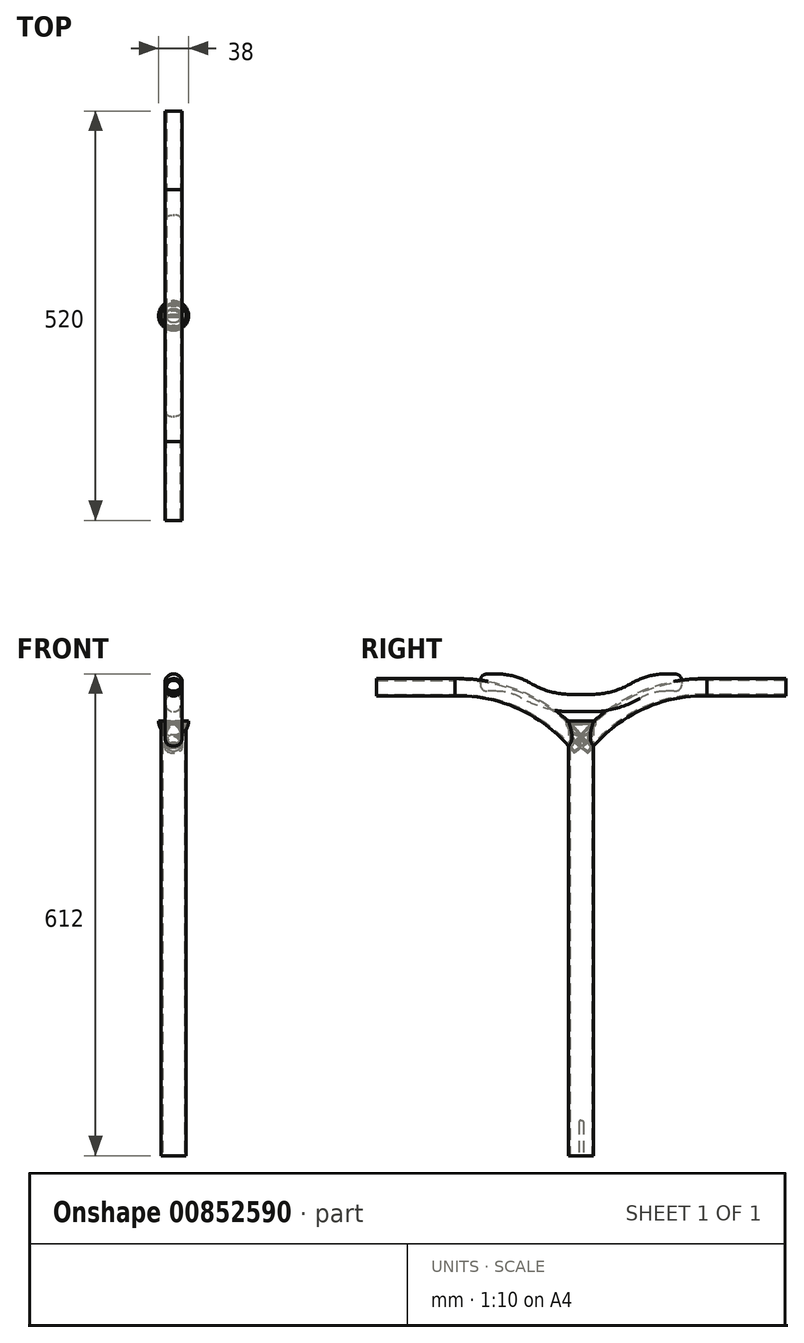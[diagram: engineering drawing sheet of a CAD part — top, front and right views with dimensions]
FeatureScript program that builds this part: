
annotation { "Feature Type Name" : "Feature", "Feature Type Description" : "" }
export const myFeature = defineFeature(function(context is Context, id is Id, definition is map)
    precondition{}
    {
        {
            var Q0;
            Q0=qCreatedBy(makeId("Top.planeOp"),FACE);
            var sketch = newSketch(context, id + "F0", { "sketchPlane" : qUnion([Q0])});
            skCircle(sketch, "E0", {"center": v(0, 0) * mm, "radius": 16 * mm});
            skSolve(sketch);
        }
        {
            var Q0;
            Q0=makeQuery(id+"F0.imprint","IMPRINT",FACE,{"disambiguationData":[TD([[makeQuery(id+"F0.imprint","IMPRINT",EDGE,{"derivedFrom":sQuery(id+"F0.wireOp",EDGE,"E0")}),1.0]])]});
            extrude(context, id + "F1", {"entities" : qUnion([Q0]), "depth" : 550 * mm, "offsetDistance" : 25 * mm});
        }
        {
            var Q0;
            Q0=makeQuery(id+"F1.opExtrude","CAP_FACE",FACE,{"disambiguationData":[OSD([sQuery(id+"F0.wireOp",EDGE,"E0")])],"isStart":true});
            shell(context, id + "F2", {"entities" : qUnion([Q0]), "thickness" : 2 * mm});
        }
        {
            var Q0;
            Q0=qCreatedBy(makeId("Right.planeOp"),FACE);
            var sketch = newSketch(context, id + "F3", { "sketchPlane" : qUnion([Q0])});
            skLineSegment(sketch, "E1.bottom", {"start": v(-2.92, 0) * mm, "end": v(3.08, 0) * mm});
            skLineSegment(sketch, "E1.top", {"start": v(0.08, 45) * mm, "end": v(0.08, 45) * mm});
            skLineSegment(sketch, "E1.left", {"start": v(-2.92, 0) * mm, "end": v(-2.92, 42) * mm});
            skLineSegment(sketch, "E1.right", {"start": v(3.08, 0) * mm, "end": v(3.08, 42) * mm});
            skPoint(sketch, "E2.visualSharp", {"position": v(-2.92, 45) * mm});
            skArc(sketch, "E2.filletArc", {"start": v(0.08, 45) * mm, "mid": v(-2.05, 44.12) * mm, "end": v(-2.92, 42) * mm});
            skPoint(sketch, "E3.visualSharp", {"position": v(3.08, 45) * mm});
            skArc(sketch, "E3.filletArc", {"start": v(3.08, 42) * mm, "mid": v(2.2, 44.12) * mm, "end": v(0.08, 45) * mm});
            skSolve(sketch);
        }
        {
            var Q0;
            Q0 = qSketchRegion(id + "F3", true);
            extrude(context, id + "F4", {"entities" : qUnion([Q0]), "operationType" : NewBodyOperationType.REMOVE, "endBound" : BoundingType.THROUGH_ALL, "oppositeDirection" : true, "depth" : 25 * mm, "offsetDistance" : 25 * mm});
        }
        {
            var Q0;
            Q0=qCreatedBy(makeId("Right.planeOp"),FACE);
            var sketch = newSketch(context, id + "F5", { "sketchPlane" : qUnion([Q0])});
            skArc(sketch, "E4", {"start": v(160, 594.94) * mm, "mid": v(70.74, 575.74) * mm, "end": v(0, 518) * mm});
            skLineSegment(sketch, "E5", {"start": v(160, 594.94) * mm, "end": v(260, 594.94) * mm});
            skSolve(sketch);
        }
        {
            var Q0;
            Q0=qCreatedBy(makeId("Front.planeOp"),FACE);
            var Q1;
            Q1=sQuery(id+"F5.wireOp",VERTEX,"E5.end");
            cPlane(context, id + "F6", {"entities" : qUnion([Q0, Q1]), "cplaneType" : CPlaneType.PLANE_POINT, "offset" : 25 * mm, "width" : 150 * mm, "height" : 150 * mm});
        }
        {
            var Q0;
            Q0=qCreatedBy(id+"F6.planeOp",FACE);
            var sketch = newSketch(context, id + "F7", { "sketchPlane" : qUnion([Q0])});
            skCircle(sketch, "E6", {"center": v(0, 594.94) * mm, "radius": 11 * mm});
            skSolve(sketch);
        }
        {
            var Q0;
            Q0=makeQuery(id+"F7.imprint","IMPRINT",FACE,{"disambiguationData":[TD([[makeQuery(id+"F7.imprint","IMPRINT",EDGE,{"derivedFrom":sQuery(id+"F7.wireOp",EDGE,"E6")}),1.0]])]});
            var Q1;
            Q1=sQuery(id+"F7.wireOp",EDGE,"E6");
            var Q2;
            Q2=sQuery(id+"F5.wireOp",EDGE,"E5");
            var Q3;
            Q3=sQuery(id+"F5.wireOp",EDGE,"E4");
            sweep(context, id + "F8", {"operationType" : NewBodyOperationType.ADD, "profiles" : qUnion([Q0]), "surfaceProfiles" : qUnion([Q1]), "path" : qUnion([Q2, Q3])});
        }
        {
            var Q0;
            Q0=makeQuery(id+"F8.opSweep","CAP_FACE",FACE,{"disambiguationData":[OSD([sQuery(id+"F5.wireOp",VERTEX,"E5.end"),sQuery(id+"F7.wireOp",EDGE,"E6")])],"isStart":true});
            shell(context, id + "F9", {"entities" : qUnion([Q0]), "thickness" : 2 * mm});
        }
        {
            var Q0;
            Q0=makeQuery(id+"F1.opExtrude","SWEPT_BODY",BODY,{"disambiguationData":[OSD([sQuery(id+"F0.wireOp",EDGE,"E0")])]});
            var Q1;
            Q1=qCreatedBy(makeId("Front.planeOp"),FACE);
            mirror(context, id + "F10", {"operationType" : NewBodyOperationType.ADD, "entities" : qUnion([Q0]), "mirrorPlane" : qUnion([Q1])});
        }
        {
            var Q0;
            Q0=qCreatedBy(makeId("Right.planeOp"),FACE);
            var sketch = newSketch(context, id + "F11", { "sketchPlane" : qUnion([Q0])});
            skArc(sketch, "E7", {"start": v(-69.28, 590.46) * mm, "mid": v(-41.92, 578.93) * mm, "end": v(-12.5, 575) * mm});
            skLineSegment(sketch, "E8", {"start": v(-12.5, 575) * mm, "end": v(0, 575) * mm});
            skArc(sketch, "E9", {"start": v(-69.28, 590.46) * mm, "mid": v(-87.93, 598.32) * mm, "end": v(-108, 601) * mm});
            skLineSegment(sketch, "E10", {"start": v(-108, 601) * mm, "end": v(-128, 601) * mm});
            skLineSegment(sketch, "E11.MirrorCS", {"start": v(12.5, 575) * mm, "end": v(0, 575) * mm});
            skArc(sketch, "E12.MirrorCS", {"start": v(69.28, 590.46) * mm, "mid": v(41.92, 578.93) * mm, "end": v(12.5, 575) * mm});
            skArc(sketch, "E13.MirrorCS", {"start": v(69.28, 590.46) * mm, "mid": v(87.93, 598.32) * mm, "end": v(108, 601) * mm});
            skLineSegment(sketch, "E14.MirrorCS", {"start": v(108, 601) * mm, "end": v(128, 601) * mm});
            skSolve(sketch);
        }
        {
            var Q0;
            Q0=sQuery(id+"F11.wireOp",VERTEX,"E14.MirrorCS.end");
            var Q1;
            Q1=qCreatedBy(id+"F6.planeOp",FACE);
            cPlane(context, id + "F12", {"entities" : qUnion([Q0, Q1]), "cplaneType" : CPlaneType.PLANE_POINT, "offset" : 25 * mm, "width" : 150 * mm, "height" : 150 * mm});
        }
        {
            var Q0;
            Q0=qCreatedBy(id+"F12.planeOp",FACE);
            var sketch = newSketch(context, id + "F13", { "sketchPlane" : qUnion([Q0])});
            skCircle(sketch, "E15", {"center": v(0, 601) * mm, "radius": 11 * mm});
            skSolve(sketch);
        }
        {
            var Q0;
            Q0=makeQuery(id+"F13.imprint","IMPRINT",FACE,{"disambiguationData":[TD([[makeQuery(id+"F13.imprint","IMPRINT",EDGE,{"derivedFrom":sQuery(id+"F13.wireOp",EDGE,"E15")}),1.0]])]});
            var Q1;
            Q1=sQuery(id+"F11.wireOp",EDGE,"E14.MirrorCS");
            var Q2;
            Q2=sQuery(id+"F11.wireOp",EDGE,"E13.MirrorCS");
            var Q3;
            Q3=sQuery(id+"F11.wireOp",EDGE,"E12.MirrorCS");
            var Q4;
            Q4=sQuery(id+"F11.wireOp",EDGE,"E11.MirrorCS");
            var Q5;
            Q5=sQuery(id+"F11.wireOp",EDGE,"E8");
            var Q6;
            Q6=sQuery(id+"F11.wireOp",EDGE,"E7");
            var Q7;
            Q7=sQuery(id+"F11.wireOp",EDGE,"E9");
            var Q8;
            Q8=sQuery(id+"F11.wireOp",EDGE,"E10");
            sweep(context, id + "F14", {"profiles" : qUnion([Q0]), "path" : qUnion([Q1, Q2, Q3, Q4, Q5, Q6, Q7, Q8])});
        }
        {
            var Q0;
            Q0=makeQuery(id+"F14.opSweep","CAP_FACE",FACE,{"disambiguationData":[OSD([sQuery(id+"F11.wireOp",VERTEX,"E10.end"),sQuery(id+"F13.wireOp",EDGE,"E15")])],"isStart":false});
            var Q1;
            Q1=makeQuery(id+"F14.opSweep","CAP_EDGE",EDGE,{"disambiguationData":[OSD([sQuery(id+"F11.wireOp",VERTEX,"E14.MirrorCS.end"),sQuery(id+"F13.wireOp",EDGE,"E15")])],"isStart":true});
            fillet(context, id + "F15", {"entities" : qUnion([Q0, Q1]), "radius" : 10 * mm, "tangentPropagation" : true, "rho" : 0.5, "crossSection" : FilletCrossSection.CONIC, "allowEdgeOverflow" : false});
        }
        {
            var Q0;
            Q0=qCreatedBy(makeId("Right.planeOp"),FACE);
            var sketch = newSketch(context, id + "F16", { "sketchPlane" : qUnion([Q0])});
            skArc(sketch, "E16", {"start": v(-19, 552) * mm, "mid": v(-13.44, 538.56) * mm, "end": v(0, 533) * mm});
            skLineSegment(sketch, "E17", {"start": v(0, 552) * mm, "end": v(0, 533) * mm});
            skLineSegment(sketch, "E18", {"start": v(0, 552) * mm, "end": v(-19, 552) * mm});
            skSolve(sketch);
        }
        {
            var Q0;
            Q0=makeQuery(id+"F16.imprint","IMPRINT",FACE,{"disambiguationData":[TD([[makeQuery(id+"F16.imprint","IMPRINT",EDGE,{"derivedFrom":sQuery(id+"F16.wireOp",EDGE,"E16")}),1.0]])]});
            var Q1;
            Q1=sQuery(id+"F16.wireOp",EDGE,"E17");
            revolve(context, id + "F17", {"surfaceOperationType" : NewSurfaceOperationType.NEW, "entities" : qUnion([Q0]), "axis" : qUnion([Q1]), "revolveType" : RevolveType.FULL});
        }
        {
            var Q0;
            Q0=makeQuery(id+"F17.opRevolve","SWEPT_FACE",FACE,{"disambiguationData":[OSD([sQuery(id+"F16.wireOp",EDGE,"E18")])]});
            shell(context, id + "F18", {"entities" : qUnion([Q0]), "thickness" : 2 * mm});
        }
    });
